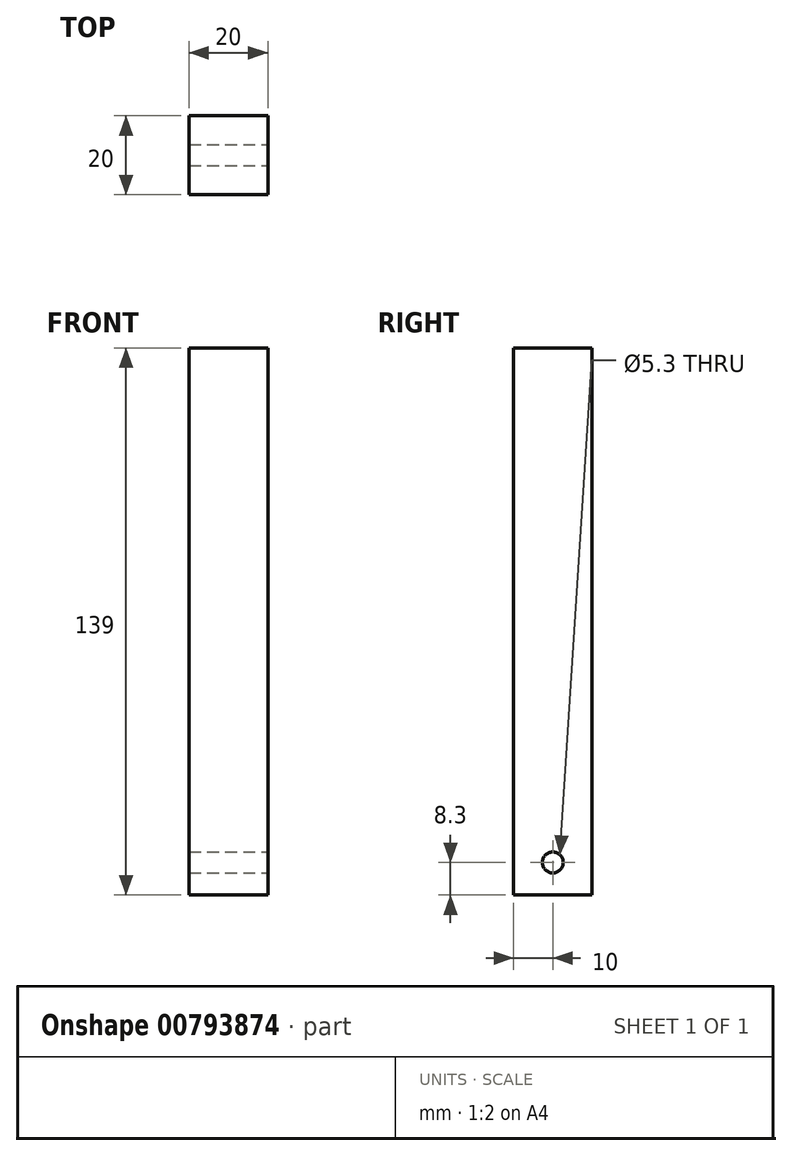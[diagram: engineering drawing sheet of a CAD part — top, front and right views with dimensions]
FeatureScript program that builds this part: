
annotation { "Feature Type Name" : "Feature", "Feature Type Description" : "" }
export const myFeature = defineFeature(function(context is Context, id is Id, definition is map)
    precondition{}
    {
        {
            var Q0;
            Q0=qCreatedBy(makeId("Top.planeOp"),FACE);
            var sketch = newSketch(context, id + "F0", { "sketchPlane" : qUnion([Q0])});
            skLineSegment(sketch, "E0.bottom", {"start": v(-10, 10) * mm, "end": v(10, 10) * mm});
            skLineSegment(sketch, "E0.top", {"start": v(-10, -10) * mm, "end": v(10, -10) * mm});
            skLineSegment(sketch, "E0.left", {"start": v(-10, 10) * mm, "end": v(-10, -10) * mm});
            skLineSegment(sketch, "E0.right", {"start": v(10, 10) * mm, "end": v(10, -10) * mm});
            skSolve(sketch);
        }
        {
            var Q0;
            Q0=qSketchRegion(id+"F0",true);
            extrude(context, id + "F1", {"entities" : qUnion([Q0]), "depth" : 139 * mm, "offsetDistance" : 25 * mm});
        }
        {
            var Q0;
            Q0=makeQuery(id+"F1.opExtrude","SWEPT_FACE",FACE,{"disambiguationData":[OSD([sQuery(id+"F0.wireOp",EDGE,"E0.right")])]});
            var sketch = newSketch(context, id + "F2", { "sketchPlane" : qUnion([Q0])});
            skCircle(sketch, "E1", {"center": v(0, 10) * mm, "radius": 2.5 * mm});
            skSolve(sketch);
        }
        {
            var Q0;
            Q0=makeQuery(id+"F2.imprint","IMPRINT",FACE,{"disambiguationData":[TD([[makeQuery(id+"F2.imprint","IMPRINT",EDGE,{"derivedFrom":sQuery(id+"F2.wireOp",EDGE,"E1")}),-1.0]])]});
            var sketch = newSketch(context, id + "F3", { "sketchPlane" : qUnion([Q0])});
            skCircle(sketch, "E2", {"center": v(0, 8.3) * mm, "radius": 2.65 * mm});
            skSolve(sketch);
        }
        {
            var Q0;
            Q0=qSketchRegion(id+"F3",true);
            extrude(context, id + "F4", {"entities" : qUnion([Q0]), "operationType" : NewBodyOperationType.REMOVE, "endBound" : BoundingType.THROUGH_ALL, "oppositeDirection" : true, "depth" : 25 * mm});
        }
    });
